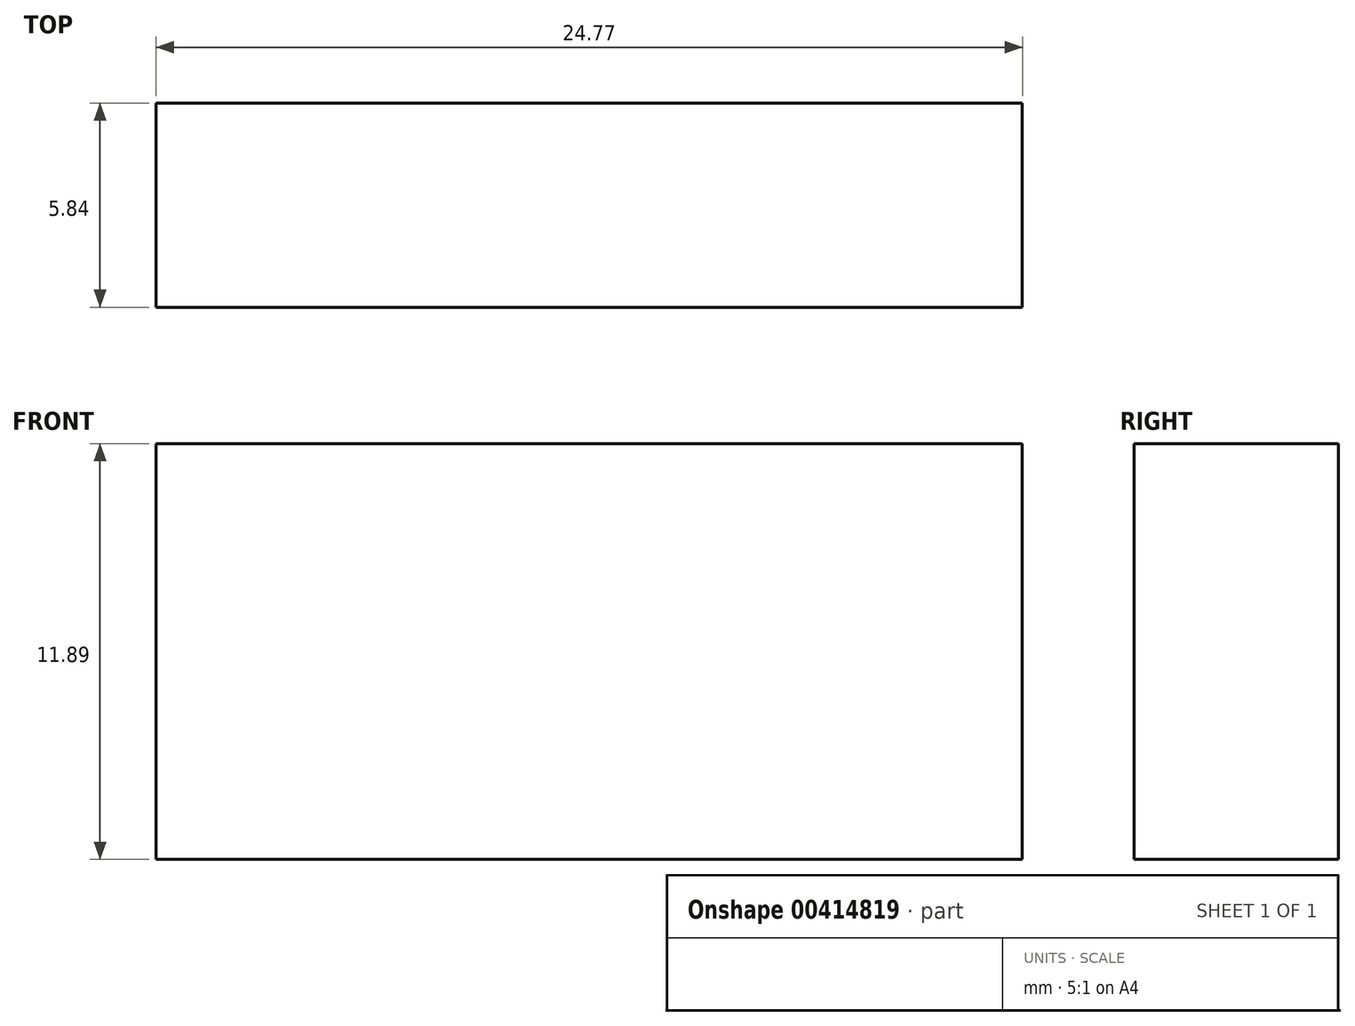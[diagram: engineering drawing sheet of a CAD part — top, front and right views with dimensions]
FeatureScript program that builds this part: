
annotation { "Feature Type Name" : "Feature", "Feature Type Description" : "" }
export const myFeature = defineFeature(function(context is Context, id is Id, definition is map)
    precondition{}
    {
        {
            var Q0;
            Q0=qCreatedBy(makeId("Front.planeOp"),FACE);
            var sketch = newSketch(context, id + "F0", { "sketchPlane" : qUnion([Q0])});
            skLineSegment(sketch, "E0.bottom", {"start": v(0, 0) * mm, "end": v(24.77, 0) * mm});
            skLineSegment(sketch, "E0.top", {"start": v(0, -11.89) * mm, "end": v(24.77, -11.89) * mm});
            skLineSegment(sketch, "E0.left", {"start": v(0, 0) * mm, "end": v(0, -11.89) * mm});
            skLineSegment(sketch, "E0.right", {"start": v(24.77, 0) * mm, "end": v(24.77, -11.89) * mm});
            skLineSegment(sketch, "E1", {"start": v(24.77, -5.94) * mm, "end": v(-51.43, -5.94) * mm, "construction": true});
            skArc(sketch, "E2", {"start": v(21.1, -11.89) * mm, "mid": v(21.59, -5.94) * mm, "end": v(21.1, 0) * mm});
            skSolve(sketch);
        }
        {
            var Q0;
            Q0 = qSketchRegion(id + "F0", true);
            extrude(context, id + "F1", {"entities" : qUnion([Q0]), "depth" : 5.84 * mm});
        }
    });
